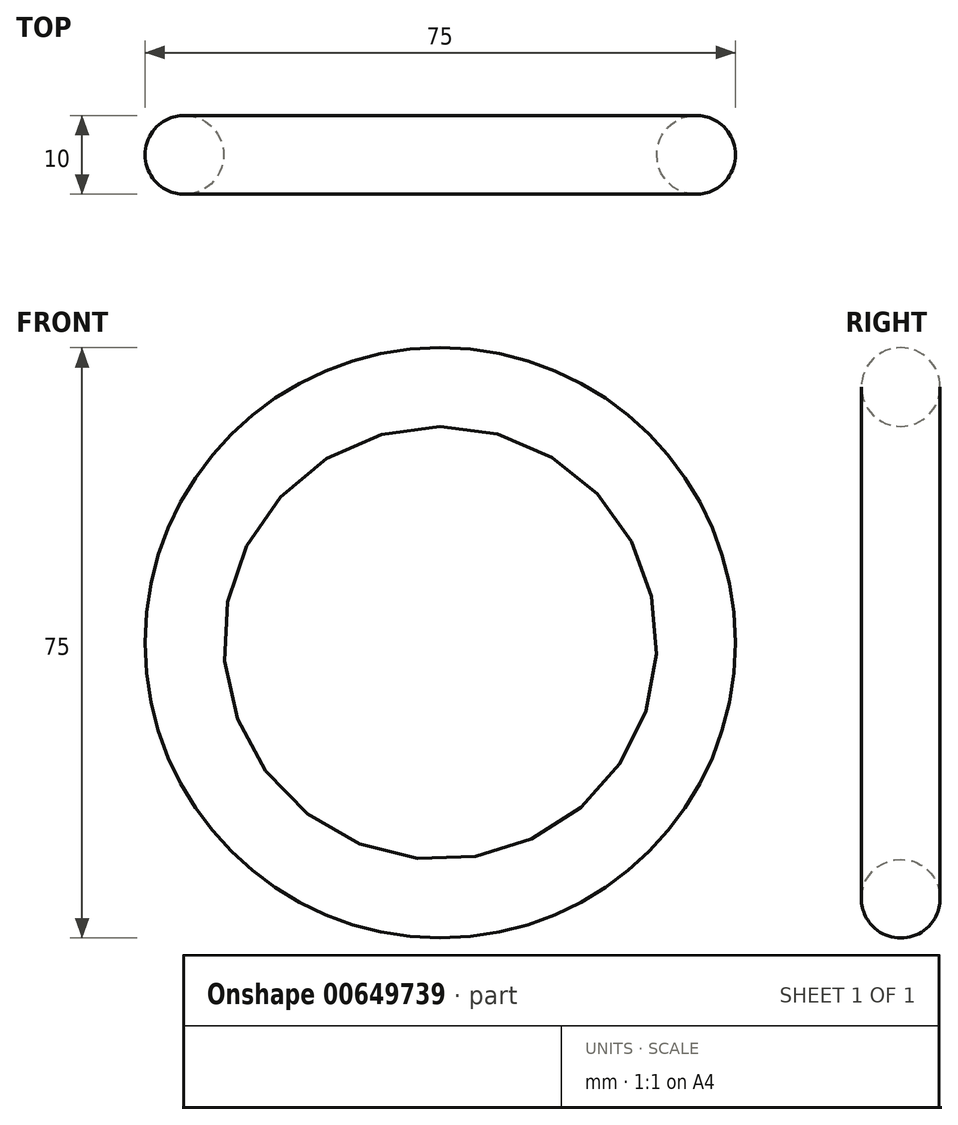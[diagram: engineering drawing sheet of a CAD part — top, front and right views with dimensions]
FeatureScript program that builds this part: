
annotation { "Feature Type Name" : "Feature", "Feature Type Description" : "" }
export const myFeature = defineFeature(function(context is Context, id is Id, definition is map)
    precondition{}
    {
        {
            var Q0;
            Q0=qCreatedBy(makeId("Top.planeOp"),FACE);
            var sketch = newSketch(context, id + "F0", { "sketchPlane" : qUnion([Q0])});
            skCircle(sketch, "E0", {"center": v(-32.5, 0) * mm, "radius": 5 * mm});
            skLineSegment(sketch, "E1", {"start": v(0, 45.09) * mm, "end": v(0, -54.91) * mm, "construction": true});
            skSolve(sketch);
        }
        {
            var Q0;
            Q0=makeQuery(id+"F0.imprint","IMPRINT",FACE,{"disambiguationData":[TD([[makeQuery(id+"F0.imprint","IMPRINT",EDGE,{"derivedFrom":sQuery(id+"F0.wireOp",EDGE,"E0")}),1.0]])]});
            var Q1;
            Q1=sQuery(id+"F0.wireOp",EDGE,"E1");
            revolve(context, id + "F1", {"entities" : qUnion([Q0]), "axis" : qUnion([Q1]), "revolveType" : RevolveType.FULL});
        }
    });
